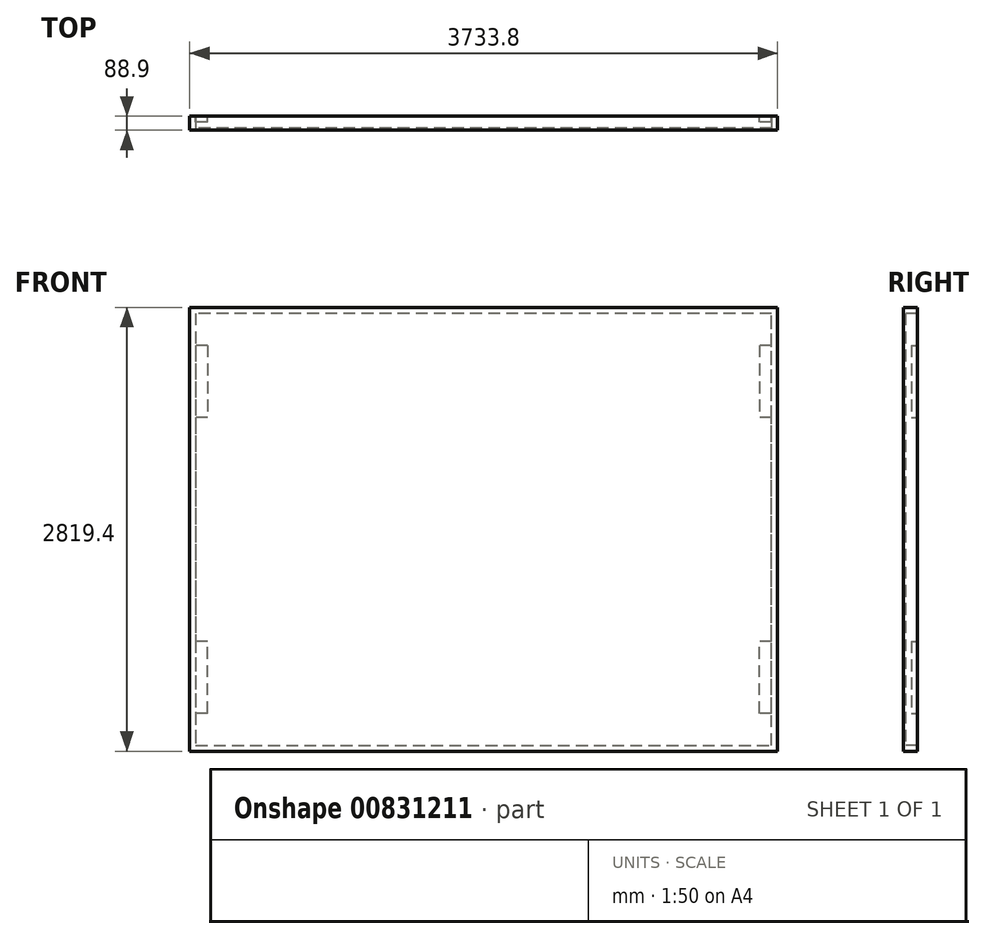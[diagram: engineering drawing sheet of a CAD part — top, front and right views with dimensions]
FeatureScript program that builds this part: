
annotation { "Feature Type Name" : "Feature", "Feature Type Description" : "" }
export const myFeature = defineFeature(function(context is Context, id is Id, definition is map)
    precondition{}
    {
        {
            var Q0;
            Q0=qCreatedBy(makeId("Front.planeOp"),FACE);
            var sketch = newSketch(context, id + "F0", { "sketchPlane" : qUnion([Q0])});
            skLineSegment(sketch, "E0.bottom", {"start": v(1866.9, 1409.7) * mm, "end": v(-1866.9, 1409.7) * mm});
            skLineSegment(sketch, "E0.left", {"start": v(1866.9, 1409.7) * mm, "end": v(1866.9, -1409.7) * mm});
            skLineSegment(sketch, "E0.right", {"start": v(-1866.9, 1409.7) * mm, "end": v(-1866.9, -1409.7) * mm});
            skPoint(sketch, "E0.middle", {"position": v(0, 0) * mm});
            skLineSegment(sketch, "E1.trimOffspring", {"start": v(1866.9, -1409.7) * mm, "end": v(-1866.9, -1409.7) * mm});
            skSolve(sketch);
        }
        {
            var Q0;
            Q0=qSketchRegion(id+"F0",true);
            extrude(context, id + "F1", {"entities" : qUnion([Q0]), "depth" : 12.7 * mm, "offsetDistance" : 25.4 * mm});
        }
        {
            var Q0;
            Q0=makeQuery(id+"F1.opExtrude","CAP_FACE",FACE,{"disambiguationData":[OSD([sQuery(id+"F0.wireOp",EDGE,"E0.bottom"),sQuery(id+"F0.wireOp",EDGE,"E0.left"),sQuery(id+"F0.wireOp",EDGE,"E0.right"),sQuery(id+"F0.wireOp",EDGE,"E1.trimOffspring")])],"isStart":true});
            var sketch = newSketch(context, id + "F2", { "sketchPlane" : qUnion([Q0])});
            skLineSegment(sketch, "E2.bottom", {"start": v(-1866.9, 1409.7) * mm, "end": v(1866.9, 1409.7) * mm});
            skLineSegment(sketch, "E2.top", {"start": v(-1866.9, 1371.6) * mm, "end": v(1866.9, 1371.6) * mm});
            skLineSegment(sketch, "E2.left", {"start": v(-1866.9, 1409.7) * mm, "end": v(-1866.9, 1371.6) * mm});
            skLineSegment(sketch, "E2.right", {"start": v(1866.9, 1409.7) * mm, "end": v(1866.9, 1371.6) * mm});
            skLineSegment(sketch, "E3.bottom", {"start": v(1866.9, 1371.6) * mm, "end": v(1828.8, 1371.6) * mm});
            skLineSegment(sketch, "E3.top", {"start": v(1866.9, -1371.6) * mm, "end": v(1828.8, -1371.6) * mm});
            skLineSegment(sketch, "E3.left", {"start": v(1866.9, 1371.6) * mm, "end": v(1866.9, -1371.6) * mm});
            skLineSegment(sketch, "E3.right", {"start": v(1828.8, 1371.6) * mm, "end": v(1828.8, -1371.6) * mm});
            skLineSegment(sketch, "E4.bottom", {"start": v(1866.9, -1371.6) * mm, "end": v(-1866.9, -1371.6) * mm});
            skLineSegment(sketch, "E4.top", {"start": v(1866.9, -1409.7) * mm, "end": v(-1866.9, -1409.7) * mm});
            skLineSegment(sketch, "E4.left", {"start": v(1866.9, -1371.6) * mm, "end": v(1866.9, -1409.7) * mm});
            skLineSegment(sketch, "E4.right", {"start": v(-1866.9, -1371.6) * mm, "end": v(-1866.9, -1409.7) * mm});
            skLineSegment(sketch, "E5.bottom", {"start": v(-1866.9, -1371.6) * mm, "end": v(-1828.8, -1371.6) * mm});
            skLineSegment(sketch, "E5.top", {"start": v(-1866.9, 1371.6) * mm, "end": v(-1828.8, 1371.6) * mm});
            skLineSegment(sketch, "E5.left", {"start": v(-1866.9, -1371.6) * mm, "end": v(-1866.9, 1371.6) * mm});
            skLineSegment(sketch, "E5.right", {"start": v(-1828.8, -1371.6) * mm, "end": v(-1828.8, 1371.6) * mm});
            skLineSegment(sketch, "E6.bottom", {"start": v(-1752.6, 1371.6) * mm, "end": v(-1714.5, 1371.6) * mm});
            skLineSegment(sketch, "E6.top", {"start": v(-1752.6, -1371.6) * mm, "end": v(-1714.5, -1371.6) * mm});
            skLineSegment(sketch, "E6.left", {"start": v(-1752.6, 1371.6) * mm, "end": v(-1752.6, -1371.6) * mm});
            skLineSegment(sketch, "E6.right", {"start": v(-1714.5, 1371.6) * mm, "end": v(-1714.5, -1371.6) * mm});
            skLineSegment(sketch, "E7.bottom", {"start": v(1752.6, 1371.6) * mm, "end": v(1714.5, 1371.6) * mm});
            skLineSegment(sketch, "E7.top", {"start": v(1752.6, -1371.6) * mm, "end": v(1714.5, -1371.6) * mm});
            skLineSegment(sketch, "E7.left", {"start": v(1752.6, 1371.6) * mm, "end": v(1752.6, -1371.6) * mm});
            skLineSegment(sketch, "E7.right", {"start": v(1714.5, 1371.6) * mm, "end": v(1714.5, -1371.6) * mm});
            skLineSegment(sketch, "E8.bottom", {"start": v(1181.1, -1371.6) * mm, "end": v(1143, -1371.6) * mm});
            skLineSegment(sketch, "E8.top", {"start": v(1181.1, 1371.6) * mm, "end": v(1143, 1371.6) * mm});
            skLineSegment(sketch, "E8.left", {"start": v(1181.1, -1371.6) * mm, "end": v(1181.1, 1371.6) * mm});
            skLineSegment(sketch, "E8.right", {"start": v(1143, -1371.6) * mm, "end": v(1143, 1371.6) * mm});
            skLineSegment(sketch, "E9.bottom", {"start": v(609.6, 1371.6) * mm, "end": v(571.5, 1371.6) * mm});
            skLineSegment(sketch, "E9.top", {"start": v(609.6, -1371.6) * mm, "end": v(571.5, -1371.6) * mm});
            skLineSegment(sketch, "E9.left", {"start": v(609.6, 1371.6) * mm, "end": v(609.6, -1371.6) * mm});
            skLineSegment(sketch, "E9.right", {"start": v(571.5, 1371.6) * mm, "end": v(571.5, -1371.6) * mm});
            skLineSegment(sketch, "E10.bottom", {"start": v(69.85, -1371.6) * mm, "end": v(31.75, -1371.6) * mm});
            skLineSegment(sketch, "E10.top", {"start": v(69.85, 1371.6) * mm, "end": v(31.75, 1371.6) * mm});
            skLineSegment(sketch, "E10.left", {"start": v(69.85, -1371.6) * mm, "end": v(69.85, 1371.6) * mm});
            skLineSegment(sketch, "E10.right", {"start": v(31.75, -1371.6) * mm, "end": v(31.75, 1371.6) * mm});
            skLineSegment(sketch, "E11.bottom", {"start": v(-571.5, 1371.6) * mm, "end": v(-609.6, 1371.6) * mm});
            skLineSegment(sketch, "E11.top", {"start": v(-571.5, -1371.6) * mm, "end": v(-609.6, -1371.6) * mm});
            skLineSegment(sketch, "E11.left", {"start": v(-571.5, 1371.6) * mm, "end": v(-571.5, -1371.6) * mm});
            skLineSegment(sketch, "E11.right", {"start": v(-609.6, 1371.6) * mm, "end": v(-609.6, -1371.6) * mm});
            skLineSegment(sketch, "E12.bottom", {"start": v(-1143, -1371.6) * mm, "end": v(-1181.1, -1371.6) * mm});
            skLineSegment(sketch, "E12.top", {"start": v(-1143, 1371.6) * mm, "end": v(-1181.1, 1371.6) * mm});
            skLineSegment(sketch, "E12.left", {"start": v(-1143, -1371.6) * mm, "end": v(-1143, 1371.6) * mm});
            skLineSegment(sketch, "E12.right", {"start": v(-1181.1, -1371.6) * mm, "end": v(-1181.1, 1371.6) * mm});
            skSolve(sketch);
        }
        {
            var Q0;
            Q0 = qSketchRegion(id + "F2", true);
            var Q1;
            Q1=makeQuery(id+"F2.imprint","IMPRINT",FACE,{"disambiguationData":[TD([[makeQuery(id+"F2.imprint","IMPRINT",EDGE,{"derivedFrom":sQuery(id+"F2.wireOp",EDGE,"E6.bottom")}),-1.0]])]});
            var Q2;
            Q2=makeQuery(id+"F2.imprint","IMPRINT",FACE,{"disambiguationData":[TD([[makeQuery(id+"F2.imprint","IMPRINT",EDGE,{"derivedFrom":sQuery(id+"F2.wireOp",EDGE,"E12.bottom")}),-1.0]])]});
            var Q3;
            Q3=makeQuery(id+"F2.imprint","IMPRINT",FACE,{"disambiguationData":[TD([[makeQuery(id+"F2.imprint","IMPRINT",EDGE,{"derivedFrom":sQuery(id+"F2.wireOp",EDGE,"E11.bottom")}),1.0]])]});
            var Q4;
            Q4=makeQuery(id+"F2.imprint","IMPRINT",FACE,{"disambiguationData":[TD([[makeQuery(id+"F2.imprint","IMPRINT",EDGE,{"derivedFrom":sQuery(id+"F2.wireOp",EDGE,"E10.bottom")}),-1.0]])]});
            var Q5;
            Q5=makeQuery(id+"F2.imprint","IMPRINT",FACE,{"disambiguationData":[TD([[makeQuery(id+"F2.imprint","IMPRINT",EDGE,{"derivedFrom":sQuery(id+"F2.wireOp",EDGE,"E9.bottom")}),1.0]])]});
            var Q6;
            Q6=makeQuery(id+"F2.imprint","IMPRINT",FACE,{"disambiguationData":[TD([[makeQuery(id+"F2.imprint","IMPRINT",EDGE,{"derivedFrom":sQuery(id+"F2.wireOp",EDGE,"E8.bottom")}),-1.0]])]});
            var Q7;
            Q7=makeQuery(id+"F2.imprint","IMPRINT",FACE,{"disambiguationData":[TD([[makeQuery(id+"F2.imprint","IMPRINT",EDGE,{"derivedFrom":sQuery(id+"F2.wireOp",EDGE,"E7.bottom")}),1.0]])]});
            extrude(context, id + "F3", {"entities" : qUnion([Q0, Q1, Q2, Q3, Q4, Q5, Q6, Q7]), "operationType" : NewBodyOperationType.ADD, "depth" : 76.2 * mm, "offsetDistance" : 25.4 * mm});
        }
        {
            var Q0;
            Q0=makeQuery(id+"F3.opExtrude","CAP_FACE",FACE,{"disambiguationData":[OSD([sQuery(id+"F2.wireOp",EDGE,"E2.bottom"),sQuery(id+"F2.wireOp",EDGE,"E2.top"),sQuery(id+"F2.wireOp",EDGE,"E2.left"),sQuery(id+"F2.wireOp",EDGE,"E2.right"),sQuery(id+"F2.wireOp",EDGE,"E3.left"),sQuery(id+"F2.wireOp",EDGE,"E3.right"),sQuery(id+"F2.wireOp",EDGE,"E4.bottom"),sQuery(id+"F2.wireOp",EDGE,"E4.top"),sQuery(id+"F2.wireOp",EDGE,"E4.left"),sQuery(id+"F2.wireOp",EDGE,"E4.right"),sQuery(id+"F2.wireOp",EDGE,"E5.left"),sQuery(id+"F2.wireOp",EDGE,"E5.right"),sQuery(id+"F2.wireOp",EDGE,"E6.left"),sQuery(id+"F2.wireOp",EDGE,"E6.right"),sQuery(id+"F2.wireOp",EDGE,"E7.left"),sQuery(id+"F2.wireOp",EDGE,"E7.right"),sQuery(id+"F2.wireOp",EDGE,"E8.left"),sQuery(id+"F2.wireOp",EDGE,"E8.right"),sQuery(id+"F2.wireOp",EDGE,"E9.left"),sQuery(id+"F2.wireOp",EDGE,"E9.right"),sQuery(id+"F2.wireOp",EDGE,"E10.left"),sQuery(id+"F2.wireOp",EDGE,"E10.right"),sQuery(id+"F2.wireOp",EDGE,"E11.left"),sQuery(id+"F2.wireOp",EDGE,"E11.right"),sQuery(id+"F2.wireOp",EDGE,"E12.left"),sQuery(id+"F2.wireOp",EDGE,"E12.right")])],"isStart":false});
            var sketch = newSketch(context, id + "F4", { "sketchPlane" : qUnion([Q0])});
            skLineSegment(sketch, "E13.bottom", {"start": v(-1828.8, 1168.4) * mm, "end": v(-1752.6, 1168.4) * mm});
            skLineSegment(sketch, "E13.top", {"start": v(-1828.8, 711.2) * mm, "end": v(-1752.6, 711.2) * mm});
            skLineSegment(sketch, "E13.left", {"start": v(-1828.8, 1168.4) * mm, "end": v(-1828.8, 711.2) * mm});
            skLineSegment(sketch, "E13.right", {"start": v(-1752.6, 1168.4) * mm, "end": v(-1752.6, 711.2) * mm});
            skLineSegment(sketch, "E14.bottom", {"start": v(-1828.8, -1168.4) * mm, "end": v(-1752.6, -1168.4) * mm});
            skLineSegment(sketch, "E14.top", {"start": v(-1828.8, -711.2) * mm, "end": v(-1752.6, -711.2) * mm});
            skLineSegment(sketch, "E14.left", {"start": v(-1828.8, -1168.4) * mm, "end": v(-1828.8, -711.2) * mm});
            skLineSegment(sketch, "E14.right", {"start": v(-1752.6, -1168.4) * mm, "end": v(-1752.6, -711.2) * mm});
            skLineSegment(sketch, "E15.bottom", {"start": v(1752.6, 1168.4) * mm, "end": v(1828.8, 1168.4) * mm});
            skLineSegment(sketch, "E15.top", {"start": v(1752.6, 711.2) * mm, "end": v(1828.8, 711.2) * mm});
            skLineSegment(sketch, "E15.left", {"start": v(1752.6, 1168.4) * mm, "end": v(1752.6, 711.2) * mm});
            skLineSegment(sketch, "E15.right", {"start": v(1828.8, 1168.4) * mm, "end": v(1828.8, 711.2) * mm});
            skLineSegment(sketch, "E16.bottom", {"start": v(1752.6, -1168.4) * mm, "end": v(1828.8, -1168.4) * mm});
            skLineSegment(sketch, "E16.top", {"start": v(1752.6, -711.2) * mm, "end": v(1828.8, -711.2) * mm});
            skLineSegment(sketch, "E16.left", {"start": v(1752.6, -1168.4) * mm, "end": v(1752.6, -711.2) * mm});
            skLineSegment(sketch, "E16.right", {"start": v(1828.8, -1168.4) * mm, "end": v(1828.8, -711.2) * mm});
            skSolve(sketch);
        }
        {
            var Q0;
            Q0 = qSketchRegion(id + "F4", true);
            extrude(context, id + "F5", {"entities" : qUnion([Q0]), "operationType" : NewBodyOperationType.ADD, "oppositeDirection" : true, "depth" : 38.1 * mm, "offsetDistance" : 25.4 * mm});
        }
    });
